# Revit family: Midea_V4+I_Outdoor_MDV-V450W_DRN1(DC50Hz)
name_source: partatom
category: Mechanical Equipment
revit_build: Autodesk Revit 2013 (Build: 20120221_2030(x64)
units: mm (PartAtom-declared; Revit-internal decimal feet)

## types (1)
- MDV-V450W/DRN1
    Air Flow = 16575.000 m³/h
    Casing color = SB2014
    Compressor = 2
    Condensation = air
    Cooling Capacity = 50 kW
    Cooling Power Input = 14 kW
    Depth = 540 mm  [stored 1.77165 ft]
    Description = High efficiency air cooled
    Gas = R410a
    Gas pipe = 25.4 mm  [stored 0.0833333 ft]
    Heating Capacity = 50 kW
    Heating Power Input = 13 kW
    Height = 1650 mm  [stored 5.41339 ft]
    Installation = outdoor installation
    Liquid pipe = 12.7 mm  [stored 0.0416667 ft]
    MCA (Minimum Circuit Amps) = 53 A
    MFA (Maximum Fuse Amps) = 60 A
    Machine material = Galvanized Steel
    Manufacturer = Midea
    Model = MDV-V450W/DRN1
    Net Weight = 275.00 kg
    Power supply = 380-415V 3N~50Hz
    Series = V4 Plus
    URL = http://cac.midea.com
    Width = 1460 mm  [stored 4.79003 ft]
    clearance access behind = 400 mm  [stored 1.31234 ft]
    clearance access front = 412 mm
    clearance access left = 600 mm
    clearance access right = 400 mm  [stored 1.31234 ft]

note: [stored X ft] marks values corroborated as IEEE doubles in the binary element streams (Revit-internal decimal feet)

## geometry (parser evidence)
native form markers: Sweep x3
no freeform markers — native parametric forms only
